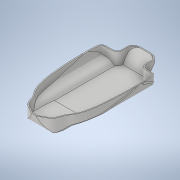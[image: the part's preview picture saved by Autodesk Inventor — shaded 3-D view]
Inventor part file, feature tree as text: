
AUTODESK INVENTOR PART (.ipt)
format: ipt  version: 2020.1 (Build 241239000, 239)  size: 989,696 bytes
history: native  units: mm
features: other x8, extrude x5, sketch x3, surface_op x2, delete_face x1, plane x1, split x1, shell x1, chamfer x1
ambient origin geometry x8: Origin, YZ Plane, XZ Plane, XY Plane, X Axis, Y Axis, Z Axis, Center Point
bodies: Body1 (feature_tree), Body2 (feature_tree), Body3 (feature_tree), Body4 (feature_tree), Body5 (feature_tree)
feature tree (23):
  other  "deck.ipt"
  other  "CrossSection1"
  other  "CrossSection2"
  delete_face  "Delete Face1"
  surface_op  "Extend3"
  plane  "Work Plane1"
  sketch  "Sketch22"  dims[d2=10.0mm d3=300.0mm d4=0.0mm d66=-41.0mm]
  sketch  "Sketch24"  dims[d110=91.75mm]
  surface_op  "Sculpt7"
  extrude  "Extrusion9"  Depth=300.0mm TaperAngle=0.0deg
  split  "Split3"
  shell  "Shell1"  Thickness=-41.0mm
  chamfer  "Chamfer1"  Distance=37.0mm
  other  "Srf1"
  other  "Front Profile"
  sketch  "Sketch25"  dims[d290=5.0mm d293=37.0mm d294=186.0mm d295=32.0mm d296=90.0mm d297=5.0mm d298=14.0mm d299=3.0mm d300=3.0mm d303=62.0mm d304=70.0mm d305=38.0mm d306=105.0mm d307=14.0mm d308=500.0mm d309=0.0mm d310=250.0mm d311=0.0mm d312=50.0mm d313=0.0mm d314=167.75mm d315=0.0mm d316=3.0mm d317=0.5mm d318=2.0mm d319=0.0mm d320=20.0mm d321=3.0mm d322=2.0mm d323=45.0deg d324=0.5mm d325=2.0mm d326=114.0mm d327=20.0mm]
  other  "Srf32"
  other  "Srf33"
  other  "Srf34"
  extrude  "ExtrusionSrf1"  Depth=186.0mm
  extrude  "ExtrusionSrf9"  Depth=32.0mm
  extrude  "ExtrusionSrf10"  Depth=90.0mm
  extrude  "ExtrusionSrf11"  Depth=5.0mm
